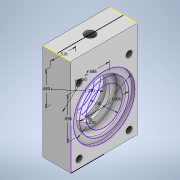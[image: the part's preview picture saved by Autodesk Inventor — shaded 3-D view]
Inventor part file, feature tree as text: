
AUTODESK INVENTOR PART (.ipt)
format: ipt  version: 2020 (Build 240168000, 168)  size: 244,736 bytes
history: native  units: in
note: dims shown in document units (in); Inventor stores cm internally (conversion verified against a paired STEP export)
features: extrude x6, sketch x5, hole x5, pattern_linear x2
ambient origin geometry x8: Origin, YZ Plane, XZ Plane, XY Plane, X Axis, Y Axis, Z Axis, Center Point
bodies: Solid1 (feature_tree)
feature tree (18):
  extrude  "Extrusion1"  Depth=0.75in
  sketch  "Sketch3"  dims[d16=1.02in d17=1.27in]
  hole  "Hole2"  [1 undecoded]
  pattern_linear  "Rectangular Pattern1"  Spacing1=0.061in  [1 undecoded]
  extrude  "Extrusion2"  Depth=0.25in
  extrude  "Extrusion3"  Depth=0.25in
  extrude  "Extrusion4"  Depth=0.25in
  sketch  "Sketch4"  dims[d18=0.54in d19=0.0in]
  extrude  "Extrusion5"  Depth=0.25in
  extrude  "Extrusion6"  Depth=0.25in
  hole  "Hole3"  [1 undecoded]
  pattern_linear  "Rectangular Pattern2"  Spacing1=0.5in  [1 undecoded]
  sketch  "Sketch5"  dims[d20=0.251in d21=0.0in]
  hole  "Hole4"  [1 undecoded]
  hole  "Hole5"  [1 undecoded]
  hole  "Hole6"  [1 undecoded]
  sketch  "Sketch1"  dims[d3=0.0in d15=0.75in]
  sketch  "Sketch7"  dims[d22=0.061in d23=0.0in d24=0.688in d25=0.85in d26=0.75in d28=1.27in d29=0.251in d30=0.0in d31=0.061in d32=0.0in d44=0.13in d45=0.325in d46=0.375in d47=0.25in d48=0.5635in d49=0.4in d50=0.0in d51=0.7874in d53=1.035in d54=0.7874in d56=1.36in d57=0.5175in d58=0.68in d59=0.13in d60=0.325in d61=0.375in d62=0.25in d63=0.5635in d64=0.4in d65=0.0in d66=0.7874in d68=1.035in d69=0.7874in d71=1.36in d72=0.0625in d73=0.75in d74=0.125in d75=0.1in d76=0.5635in d77=1.0in d78=0.0in d79=0.211in d80=0.2in d81=0.125in d82=0.1in d83=0.5635in d84=0.25in d85=0.0in d88=0.211in d89=0.2in d90=0.125in d91=0.1in d92=0.5635in d93=0.25in d94=0.0in d2=0.5in d4=0.5in d5=0.0344in]
note: 7 required parameter values undecoded (feature->parameter linkage not recoverable at this tier; creation-order binding heuristic only, values carry confidence <= 0.55)
